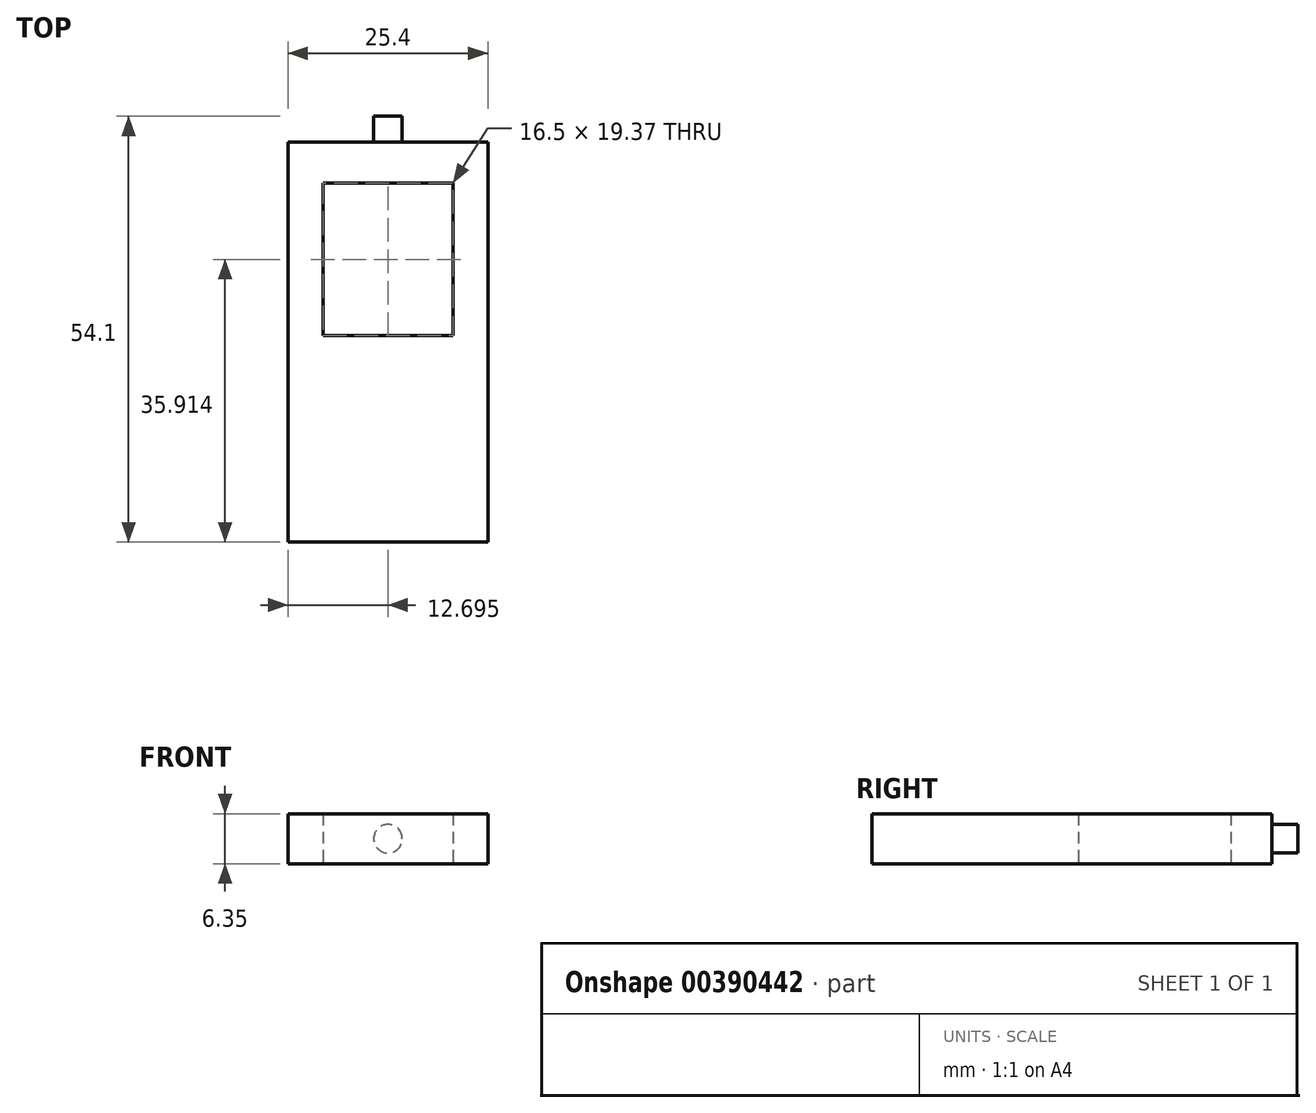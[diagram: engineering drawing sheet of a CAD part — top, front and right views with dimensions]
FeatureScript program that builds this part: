
annotation { "Feature Type Name" : "Feature", "Feature Type Description" : "" }
export const myFeature = defineFeature(function(context is Context, id is Id, definition is map)
    precondition{}
    {
        {
            var Q0;
            Q0=qCreatedBy(makeId("Top.planeOp"),FACE);
            var sketch = newSketch(context, id + "F0", { "sketchPlane" : qUnion([Q0])});
            skLineSegment(sketch, "E0.bottom", {"start": v(12.7, 25.4) * mm, "end": v(-12.7, 25.4) * mm});
            skLineSegment(sketch, "E0.top", {"start": v(12.7, -25.4) * mm, "end": v(-12.7, -25.4) * mm});
            skLineSegment(sketch, "E0.left", {"start": v(12.7, 25.4) * mm, "end": v(12.7, -25.4) * mm});
            skLineSegment(sketch, "E0.right", {"start": v(-12.7, 25.4) * mm, "end": v(-12.7, -25.4) * mm});
            skPoint(sketch, "E0.middle", {"position": v(0, 0) * mm});
            skLineSegment(sketch, "E1.bottom", {"start": v(-8.26, 20.2) * mm, "end": v(8.24, 20.2) * mm});
            skLineSegment(sketch, "E1.top", {"start": v(-8.25, 0.83) * mm, "end": v(8.24, 0.83) * mm});
            skLineSegment(sketch, "E1.left", {"start": v(-8.26, 20.2) * mm, "end": v(-8.25, 0.83) * mm});
            skLineSegment(sketch, "E1.right", {"start": v(8.25, 20.2) * mm, "end": v(8.25, 0.83) * mm});
            skSolve(sketch);
        }
        {
            var Q0;
            Q0 = qSketchRegion(id + "F0", true);
            extrude(context, id + "F1", {"entities" : qUnion([Q0]), "depth" : 6.35 * mm});
        }
        {
            var Q0;
            Q0=makeQuery(id+"F1.opExtrude","SWEPT_FACE",FACE,{"disambiguationData":[OSD([sQuery(id+"F0.wireOp",EDGE,"E0.bottom")])]});
            var sketch = newSketch(context, id + "F2", { "sketchPlane" : qUnion([Q0])});
            skCircle(sketch, "E2", {"center": v(0, 3.18) * mm, "radius": 1.81 * mm});
            skSolve(sketch);
        }
        {
            var Q0;
            Q0 = qSketchRegion(id + "F2", true);
            extrude(context, id + "F3", {"entities" : qUnion([Q0]), "operationType" : NewBodyOperationType.ADD, "depth" : 3.3 * mm});
        }
    });
